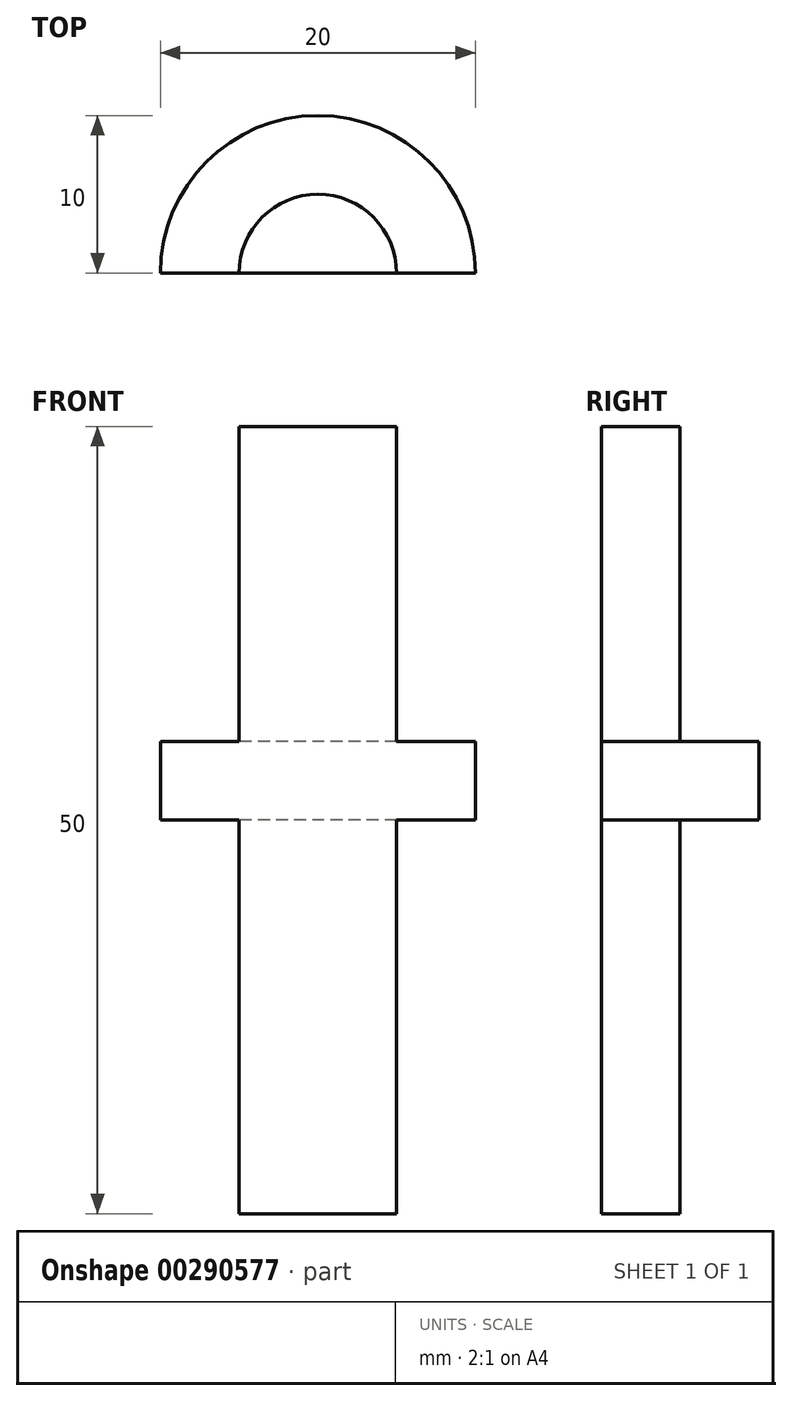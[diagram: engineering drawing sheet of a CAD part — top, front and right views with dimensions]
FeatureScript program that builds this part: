
annotation { "Feature Type Name" : "Feature", "Feature Type Description" : "" }
export const myFeature = defineFeature(function(context is Context, id is Id, definition is map)
    precondition{}
    {
        {
            var Q0;
            Q0=qCreatedBy(makeId("Front.planeOp"),FACE);
            var sketch = newSketch(context, id + "F0", { "sketchPlane" : qUnion([Q0])});
            skLineSegment(sketch, "E0.bottom", {"start": v(-5, 50) * mm, "end": v(0, 50) * mm});
            skLineSegment(sketch, "E0.top", {"start": v(-5, 0) * mm, "end": v(0, 0) * mm});
            skLineSegment(sketch, "E0.left", {"start": v(-5, 50) * mm, "end": v(-5, 30) * mm});
            skLineSegment(sketch, "E0.right", {"start": v(0, 50) * mm, "end": v(0, 0) * mm});
            skLineSegment(sketch, "E1.bottom", {"start": v(-10, 30) * mm, "end": v(-5, 30) * mm});
            skLineSegment(sketch, "E1.top", {"start": v(-10, 25) * mm, "end": v(-5, 25) * mm});
            skLineSegment(sketch, "E1.left", {"start": v(-10, 30) * mm, "end": v(-10, 25) * mm});
            skLineSegment(sketch, "E2.trimOffspring", {"start": v(-5, 25) * mm, "end": v(-5, 0) * mm});
            skSolve(sketch);
        }
        {
            var Q0;
            Q0 = qSketchRegion(id + "F0", true);
            var Q1;
            Q1=sQuery(id+"F0.wireOp",EDGE,"E0.right");
            revolve(context, id + "F1", {"entities" : qUnion([Q0]), "axis" : qUnion([Q1]), "revolveType" : RevolveType.ONE_DIRECTION, "angle" : 180 * degree});
        }
    });
